# Revit family: Restraints_Serco_SL-Manual-Wall
name_source: partatom
category: Generic Models
units: mm (PartAtom-declared; Revit-internal decimal feet)

## family parameters
Can host rebar = No
Cut with Voids When Loaded = No
Host = Face
Maintain Annotation Orientation = No
Part Type = Normal
Room Calculation Point = No
Round Connector Dimension = Use Diameter
Shared = No

## types (8) — shared parameters
Default Elevation = 4' - 0"
Description = Manual Vehicle Restraint
Manufacturer = Serco Entrematic
Model = SL10, SL20, SL40
Type Comments = Wall Mount
URL = https://sercoentrematic.com

## per-type parameters (varying)
| type | BPlateHeight | StandOff |
| No Standoff | 1' - 11 1/2" | 0' - 0" |
| No Standoff, Max. Cut-Down | 1' - 5" | 0' - 0" |
| 2" Standoff | 1' - 11 1/2" | 0' - 2" |
| 2" Standoff, Max. Cut-Down | 1' - 5" | 0' - 2" |
| 12" Standoff | 1' - 11 1/2" | 1' - 0" |
| 12" Standoff, Max. Cut-Down | 1' - 5" | 1' - 0" |
| 14" Standoff | 1' - 11 1/2" | 1' - 2" |
| 14" Standoff, Max. Cut-Down | 1' - 5" | 1' - 2" |

## geometry (parser evidence)
native form markers: Sweep x2
no freeform markers — native parametric forms only
